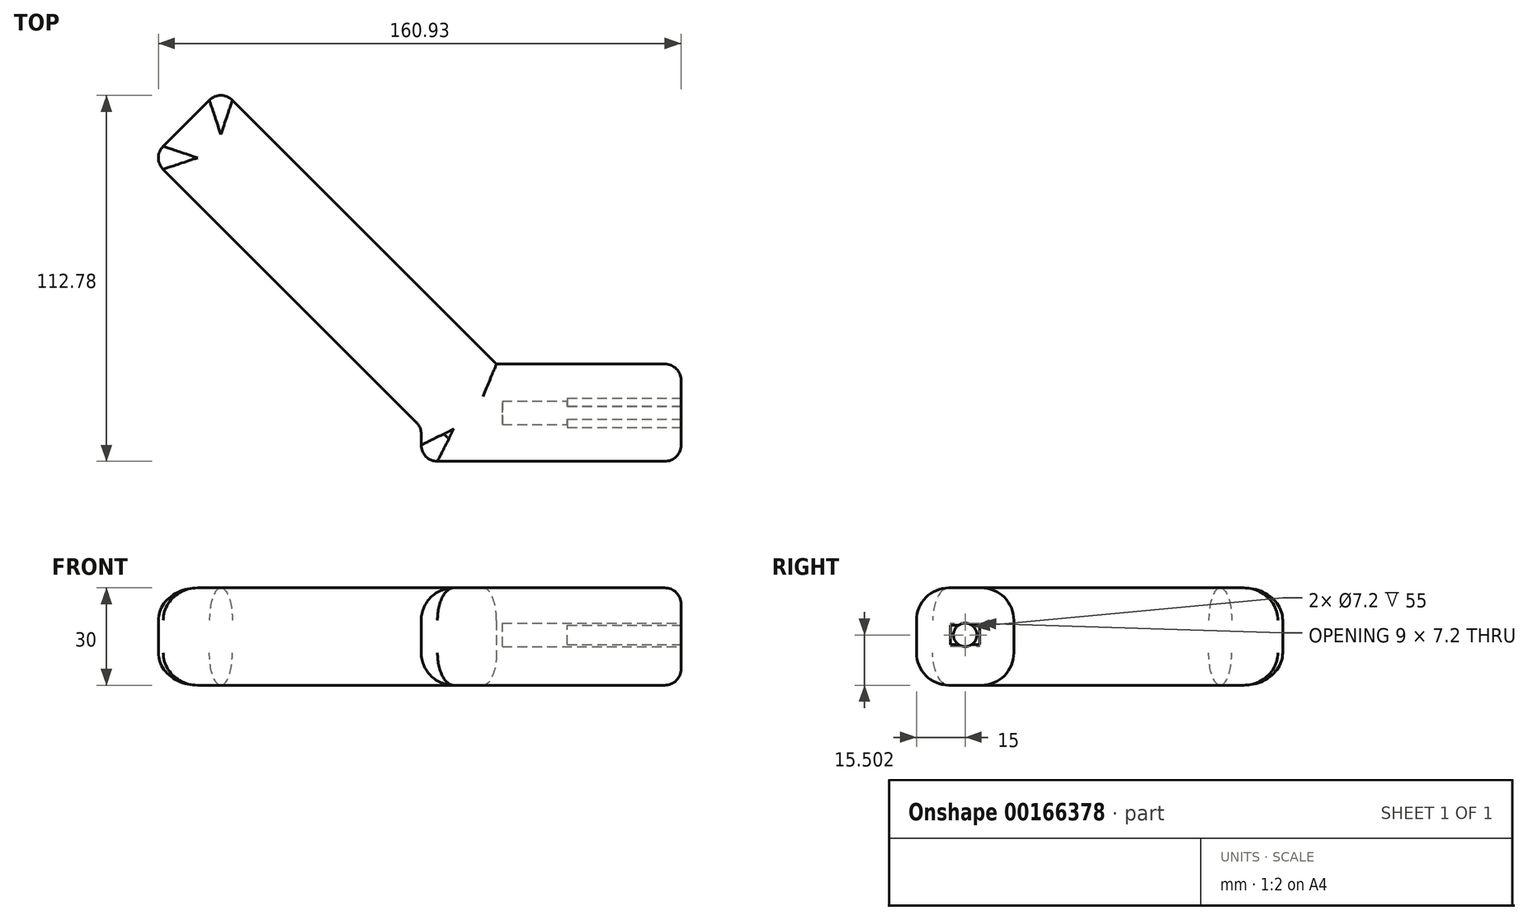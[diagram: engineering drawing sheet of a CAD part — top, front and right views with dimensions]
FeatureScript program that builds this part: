
annotation { "Feature Type Name" : "Feature", "Feature Type Description" : "" }
export const myFeature = defineFeature(function(context is Context, id is Id, definition is map)
    precondition{}
    {
        {
            var Q0;
            Q0=qCreatedBy(makeId("Top.planeOp"),FACE);
            var sketch = newSketch(context, id + "F0", { "sketchPlane" : qUnion([Q0])});
            skLineSegment(sketch, "E0.bottom", {"start": v(40, -15) * mm, "end": v(-40, -15) * mm});
            skLineSegment(sketch, "E0.top", {"start": v(40, 15) * mm, "end": v(-40, 15) * mm});
            skLineSegment(sketch, "E0.left", {"start": v(40, -15) * mm, "end": v(40, 15) * mm});
            skLineSegment(sketch, "E0.right", {"start": v(-40, -15) * mm, "end": v(-40, 15) * mm});
            skPoint(sketch, "E0.middle", {"position": v(0, 0) * mm});
            skLineSegment(sketch, "E1", {"start": v(-16.84, 15) * mm, "end": v(-101.7, 99.85) * mm});
            skLineSegment(sketch, "E2", {"start": v(-101.7, 99.85) * mm, "end": v(-123, 78.55) * mm});
            skLineSegment(sketch, "E3", {"start": v(-123, 78.55) * mm, "end": v(-40, -4.45) * mm});
            skSolve(sketch);
        }
        {
            var Q0;
            Q0 = qSketchRegion(id + "F0", true);
            extrude(context, id + "F1", {"entities" : qUnion([Q0]), "depth" : 30 * mm});
        }
        {
            var Q0;
            Q0=makeQuery(id+"F1.opExtrude","SWEPT_EDGE",EDGE,{"disambiguationData":[OSD([sQuery(id+"F0.wireOp",EDGE,"E0.bottom"),sQuery(id+"F0.wireOp",EDGE,"E0.right")])]});
            var Q1;
            Q1=makeQuery(id+"F1.opExtrude","SWEPT_EDGE",EDGE,{"disambiguationData":[OSD([sQuery(id+"F0.wireOp",EDGE,"E0.right"),sQuery(id+"F0.wireOp",EDGE,"E3")])]});
            var Q2;
            Q2=makeQuery(id+"F1.opExtrude","SWEPT_EDGE",EDGE,{"disambiguationData":[OSD([sQuery(id+"F0.wireOp",EDGE,"E2"),sQuery(id+"F0.wireOp",EDGE,"E3")])]});
            var Q3;
            Q3=makeQuery(id+"F1.opExtrude","SWEPT_EDGE",EDGE,{"disambiguationData":[OSD([sQuery(id+"F0.wireOp",EDGE,"E1"),sQuery(id+"F0.wireOp",EDGE,"E2")])]});
            var Q4;
            Q4=makeQuery(id+"F1.opExtrude","SWEPT_EDGE",EDGE,{"disambiguationData":[OSD([sQuery(id+"F0.wireOp",EDGE,"E0.top"),sQuery(id+"F0.wireOp",EDGE,"E0.left")])]});
            var Q5;
            Q5=makeQuery(id+"F1.opExtrude","SWEPT_EDGE",EDGE,{"disambiguationData":[OSD([sQuery(id+"F0.wireOp",EDGE,"E0.bottom"),sQuery(id+"F0.wireOp",EDGE,"E0.left")])]});
            var Q6;
            Q6=makeQuery(id+"F1.opExtrude","CAP_EDGE",EDGE,{"disambiguationData":[OSD([sQuery(id+"F0.wireOp",EDGE,"E0.left")])],"isStart":false});
            var Q7;
            Q7=makeQuery(id+"F1.opExtrude","CAP_EDGE",EDGE,{"disambiguationData":[OSD([sQuery(id+"F0.wireOp",EDGE,"E0.left")])],"isStart":true});
            fillet(context, id + "F2", {"entities" : qUnion([Q0, Q1, Q2, Q3, Q4, Q5, Q6, Q7]), "radius" : 5 * mm, "tangentPropagation" : true, "allowEdgeOverflow" : false});
        }
        {
            var Q0;
            Q0=makeQuery(id+"F1.opExtrude","CAP_EDGE",EDGE,{"disambiguationData":[OSD([sQuery(id+"F0.wireOp",EDGE,"E3")])],"isStart":true});
            var Q1;
            Q1=makeQuery(id+"F1.opExtrude","CAP_EDGE",EDGE,{"disambiguationData":[OSD([sQuery(id+"F0.wireOp",EDGE,"E3")])],"isStart":false});
            var Q2;
            Q2=makeQuery(id+"F1.opExtrude","CAP_EDGE",EDGE,{"disambiguationData":[OSD([sQuery(id+"F0.wireOp",EDGE,"E0.top")])],"isStart":false});
            var Q3;
            Q3=makeQuery(id+"F1.opExtrude","CAP_EDGE",EDGE,{"disambiguationData":[OSD([sQuery(id+"F0.wireOp",EDGE,"E0.top")])],"isStart":true});
            fillet(context, id + "F3", {"entities" : qUnion([Q0, Q1, Q2, Q3]), "radius" : 10 * mm, "tangentPropagation" : true, "allowEdgeOverflow" : false});
        }
        {
            var Q0;
            Q0=makeQuery(id+"F1.opExtrude","SWEPT_FACE",FACE,{"disambiguationData":[OSD([sQuery(id+"F0.wireOp",EDGE,"E0.left")])]});
            var sketch = newSketch(context, id + "F4", { "sketchPlane" : qUnion([Q0])});
            skLineSegment(sketch, "E4.bottom", {"start": v(4.5, 12.49) * mm, "end": v(-4.5, 12.49) * mm});
            skLineSegment(sketch, "E4.top", {"start": v(4.5, 18.49) * mm, "end": v(-4.5, 18.49) * mm});
            skLineSegment(sketch, "E4.left", {"start": v(4.5, 12.49) * mm, "end": v(4.5, 18.49) * mm});
            skLineSegment(sketch, "E4.right", {"start": v(-4.5, 12.49) * mm, "end": v(-4.5, 18.49) * mm});
            skPoint(sketch, "E4.middle", {"position": v(0, 15.49) * mm});
            skSolve(sketch);
        }
        {
            var Q0;
            Q0 = qSketchRegion(id + "F4", true);
            extrude(context, id + "F5", {"entities" : qUnion([Q0]), "operationType" : NewBodyOperationType.REMOVE, "oppositeDirection" : true, "depth" : 35 * mm});
        }
        {
            var Q0;
            Q0=makeQuery(id+"F5.boolean.opBoolean","COPY",FACE,{"derivedFrom":makeQuery(id+"F5.opExtrude","CAP_FACE",FACE,{"disambiguationData":[OSD([sQuery(id+"F4.wireOp",EDGE,"E4.bottom"),sQuery(id+"F4.wireOp",EDGE,"E4.top"),sQuery(id+"F4.wireOp",EDGE,"E4.left"),sQuery(id+"F4.wireOp",EDGE,"E4.right")])],"isStart":false})});
            var sketch = newSketch(context, id + "F6", { "sketchPlane" : qUnion([Q0])});
            skCircle(sketch, "E5", {"center": v(0, 15.5) * mm, "radius": 3.6 * mm});
            skSolve(sketch);
        }
        {
            var Q0;
            Q0 = qSketchRegion(id + "F6", true);
            extrude(context, id + "F7", {"entities" : qUnion([Q0]), "operationType" : NewBodyOperationType.REMOVE, "oppositeDirection" : true, "depth" : 20 * mm, "hasSecondDirection" : true, "secondDirectionOppositeDirection" : false, "secondDirectionDepth" : 40 * mm});
        }
    });
